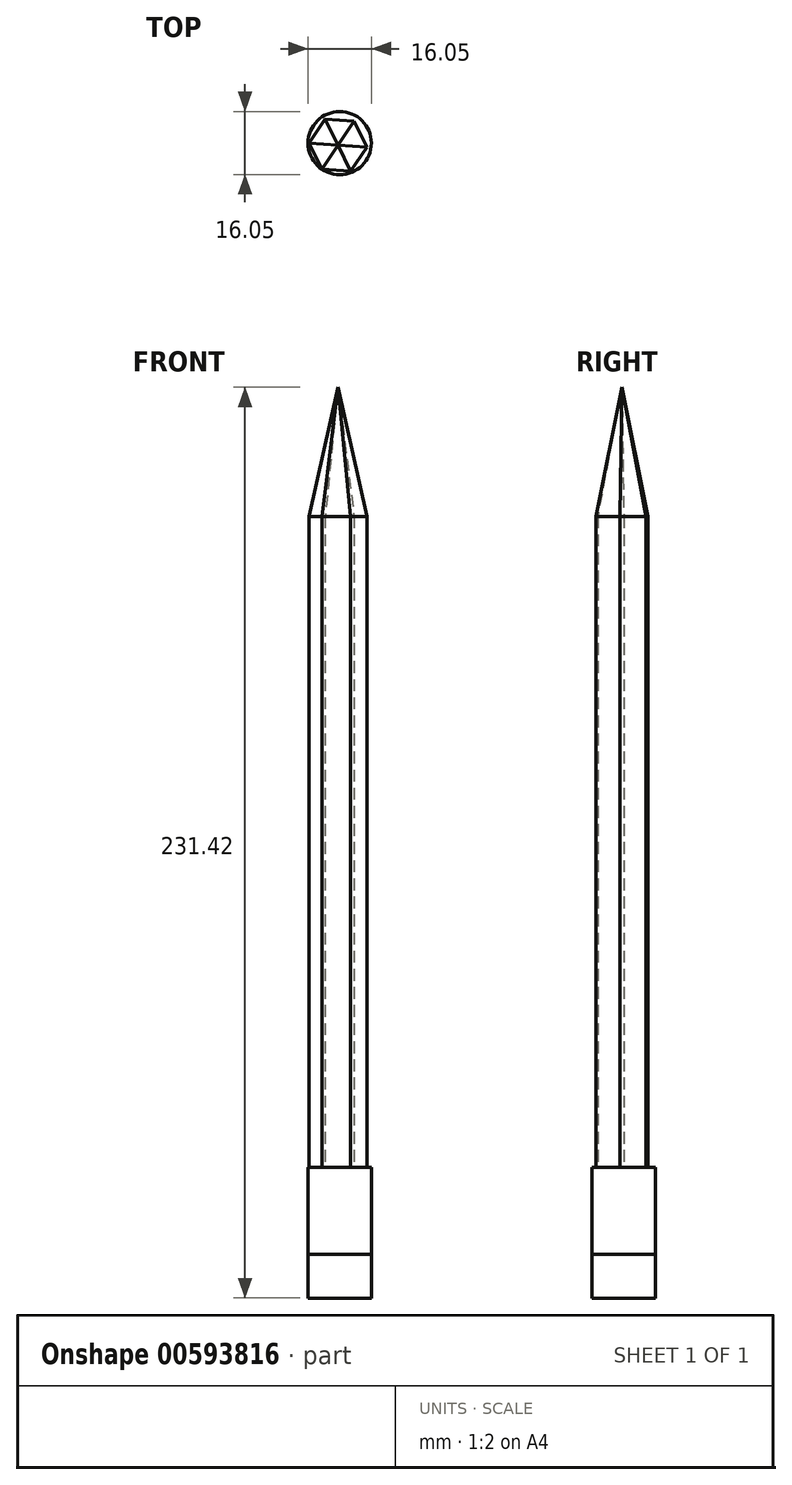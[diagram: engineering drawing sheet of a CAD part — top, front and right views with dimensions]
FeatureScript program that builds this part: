
annotation { "Feature Type Name" : "Feature", "Feature Type Description" : "" }
export const myFeature = defineFeature(function(context is Context, id is Id, definition is map)
    precondition{}
    {
        {
            var Q0;
            Q0=qCreatedBy(makeId("Top.planeOp"),FACE);
            var sketch = newSketch(context, id + "F0", { "sketchPlane" : qUnion([Q0])});
            skCircle(sketch, "E0.cCircle", {"center": v(-65.8, 0) * mm, "radius": 6.37 * mm, "construction": true});
            skLineSegment(sketch, "E0.0", {"start": v(-58.47, -0.5) * mm, "end": v(-62.58, -6.61) * mm});
            skLineSegment(sketch, "E0.1", {"start": v(-62.58, -6.61) * mm, "end": v(-69.92, -6.1) * mm});
            skLineSegment(sketch, "E0.2", {"start": v(-69.92, -6.1) * mm, "end": v(-73.15, 0.5) * mm});
            skLineSegment(sketch, "E0.3", {"start": v(-73.15, 0.5) * mm, "end": v(-69.04, 6.61) * mm});
            skLineSegment(sketch, "E0.4", {"start": v(-69.04, 6.61) * mm, "end": v(-61.7, 6.1) * mm});
            skLineSegment(sketch, "E0.5", {"start": v(-61.7, 6.1) * mm, "end": v(-58.47, -0.5) * mm});
            skPoint(sketch, "E0.0.midPoint", {"position": v(-60.52, -3.56) * mm});
            skSolve(sketch);
        }
        {
            var Q0;
            Q0=makeQuery(id+"F0.imprint","IMPRINT",FACE,{"disambiguationData":[TD([[makeQuery(id+"F0.imprint","IMPRINT",EDGE,{"derivedFrom":sQuery(id+"F0.wireOp",EDGE,"E0.0")}),-1.0]])]});
            extrude(context, id + "F1", {"entities" : qUnion([Q0]), "depth" : 165.35 * mm, "offsetDistance" : 25.4 * mm});
        }
        {
            var Q0;
            Q0=makeQuery(id+"F1.opExtrude","CAP_FACE",FACE,{"disambiguationData":[OSD([sQuery(id+"F0.wireOp",EDGE,"E0.0"),sQuery(id+"F0.wireOp",EDGE,"E0.1"),sQuery(id+"F0.wireOp",EDGE,"E0.2"),sQuery(id+"F0.wireOp",EDGE,"E0.3"),sQuery(id+"F0.wireOp",EDGE,"E0.4"),sQuery(id+"F0.wireOp",EDGE,"E0.5")])],"isStart":true});
            var sketch = newSketch(context, id + "F2", { "sketchPlane" : qUnion([Q0])});
            skCircle(sketch, "E1", {"center": v(-65.37, -0.5) * mm, "radius": 8.02 * mm});
            skPoint(sketch, "E1.centerSnap0", {"position": v(-65.37, -6.36) * mm});
            skSolve(sketch);
        }
        {
            var Q0;
            Q0 = qSketchRegion(id + "F2", true);
            extrude(context, id + "F3", {"entities" : qUnion([Q0]), "operationType" : NewBodyOperationType.ADD, "depth" : 22.1 * mm, "offsetDistance" : 25.4 * mm});
        }
        {
            var Q0;
            Q0=makeQuery(id+"F1.opExtrude","CAP_FACE",FACE,{"disambiguationData":[OSD([sQuery(id+"F0.wireOp",EDGE,"E0.0"),sQuery(id+"F0.wireOp",EDGE,"E0.1"),sQuery(id+"F0.wireOp",EDGE,"E0.2"),sQuery(id+"F0.wireOp",EDGE,"E0.3"),sQuery(id+"F0.wireOp",EDGE,"E0.4"),sQuery(id+"F0.wireOp",EDGE,"E0.5")])],"isStart":false});
            extrude(context, id + "F4", {"entities" : qUnion([Q0]), "operationType" : NewBodyOperationType.ADD, "depth" : 34.54 * mm, "offsetDistance" : 25.4 * mm, "hasDraft" : true, "draftAngle" : 11 * degree, "draftPullDirection" : true});
        }
        {
            var Q0;
            Q0=makeQuery(id+"F3.opExtrude","CAP_FACE",FACE,{"disambiguationData":[OSD([sQuery(id+"F2.wireOp",EDGE,"E1")])],"isStart":false});
            var sketch = newSketch(context, id + "F5", { "sketchPlane" : qUnion([Q0])});
            skSolve(sketch);
        }
        {
            var Q0;
            Q0=makeQuery(id+"F5.imprint","IMPRINT",FACE,{"disambiguationData":[TD([[makeQuery(id+"F5.imprint","IMPRINT",EDGE,{"derivedFrom":makeQuery(id+"F3.opExtrude","CAP_EDGE",EDGE,{"disambiguationData":[OSD([sQuery(id+"F2.wireOp",EDGE,"E1")])],"isStart":false})}),1.0]])]});
            extrude(context, id + "F6", {"entities" : qUnion([Q0]), "depth" : 11.18 * mm, "offsetDistance" : 25.4 * mm});
        }
    });
